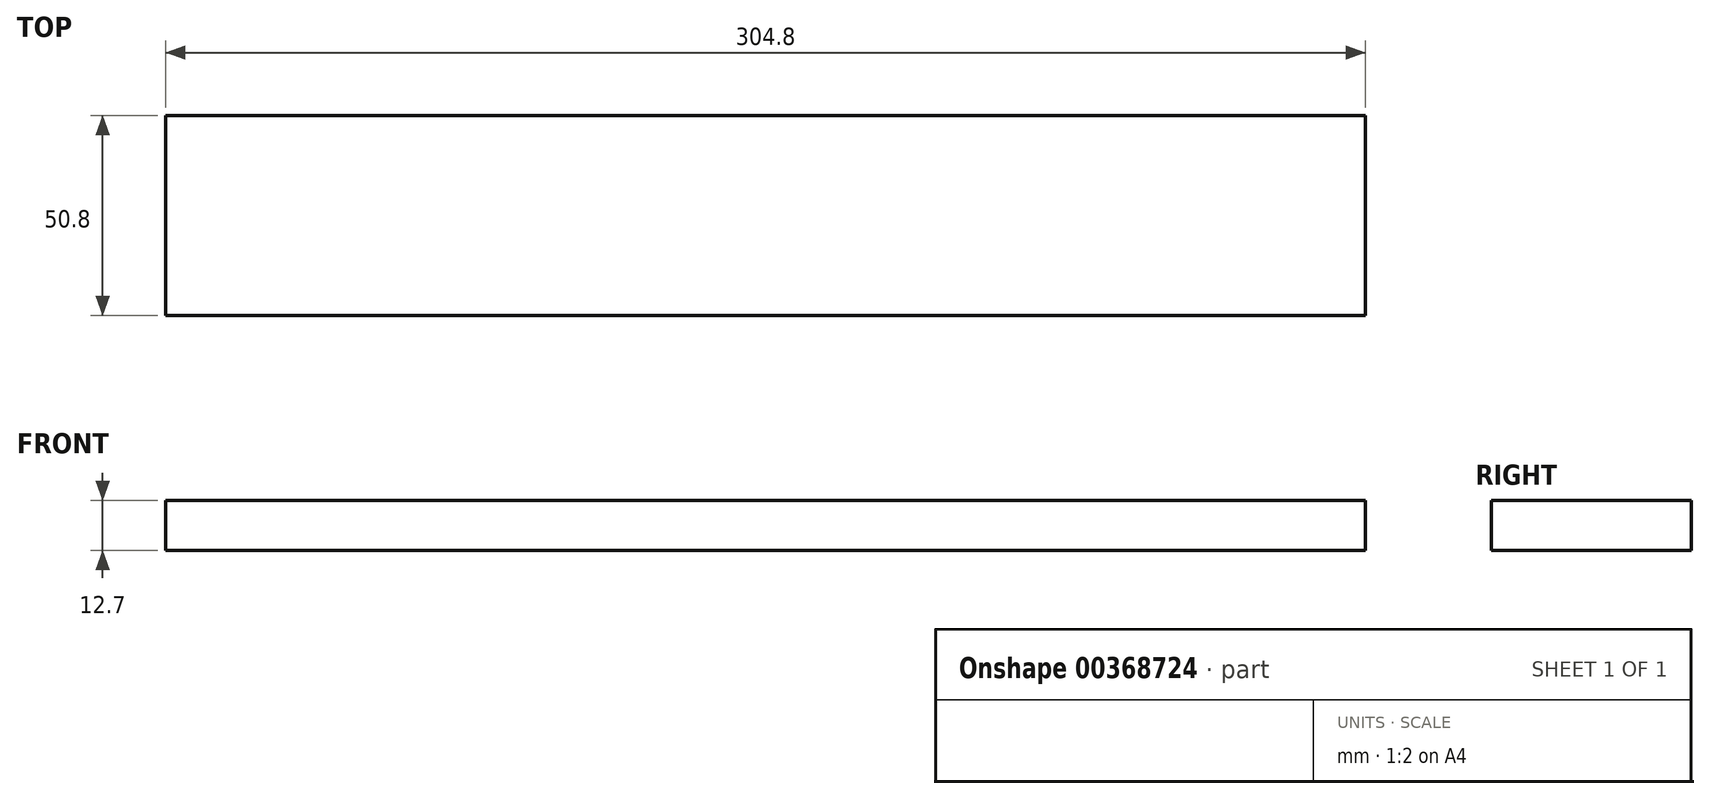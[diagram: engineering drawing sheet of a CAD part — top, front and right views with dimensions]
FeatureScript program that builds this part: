
annotation { "Feature Type Name" : "Feature", "Feature Type Description" : "" }
export const myFeature = defineFeature(function(context is Context, id is Id, definition is map)
    precondition{}
    {
        {
            var Q0;
            Q0=qCreatedBy(makeId("Top.planeOp"),FACE);
            var sketch = newSketch(context, id + "F0", { "sketchPlane" : qUnion([Q0])});
            skLineSegment(sketch, "E0.bottom", {"start": v(152.4, 25.4) * mm, "end": v(-152.4, 25.4) * mm});
            skLineSegment(sketch, "E0.top", {"start": v(152.4, -25.4) * mm, "end": v(-152.4, -25.4) * mm});
            skLineSegment(sketch, "E0.left", {"start": v(152.4, 25.4) * mm, "end": v(152.4, -25.4) * mm});
            skLineSegment(sketch, "E0.right", {"start": v(-152.4, 25.4) * mm, "end": v(-152.4, -25.4) * mm});
            skPoint(sketch, "E0.middle", {"position": v(0, 0) * mm});
            skSolve(sketch);
        }
        {
            var Q0;
            Q0=makeQuery(id+"F0.imprint","IMPRINT",FACE,{"disambiguationData":[TD([[makeQuery(id+"F0.imprint","IMPRINT",EDGE,{"derivedFrom":sQuery(id+"F0.wireOp",EDGE,"E0.bottom")}),1.0]])]});
            extrude(context, id + "F1", {"entities" : qUnion([Q0]), "depth" : 12.7 * mm});
        }
    });
